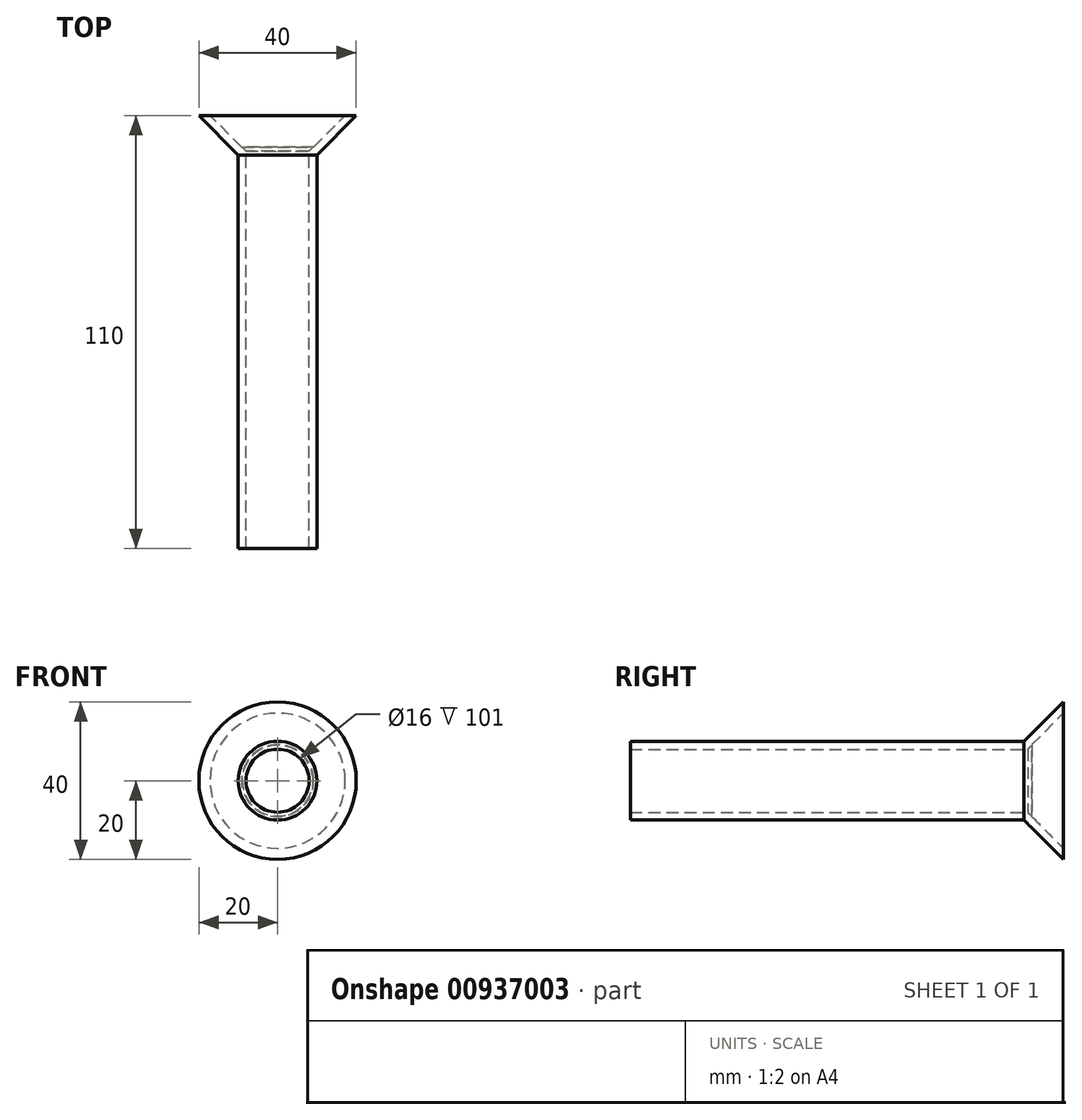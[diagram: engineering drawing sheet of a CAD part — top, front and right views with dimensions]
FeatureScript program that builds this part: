
annotation { "Feature Type Name" : "Feature", "Feature Type Description" : "" }
export const myFeature = defineFeature(function(context is Context, id is Id, definition is map)
    precondition{}
    {
        {
            var Q0;
            Q0=qCreatedBy(makeId("Front.planeOp"),FACE);
            var sketch = newSketch(context, id + "F0", { "sketchPlane" : qUnion([Q0])});
            skCircle(sketch, "E0", {"center": v(0, 0) * mm, "radius": 8 * mm});
            skCircle(sketch, "E1", {"center": v(0, 0) * mm, "radius": 10 * mm});
            skSolve(sketch);
        }
        {
            var Q0;
            Q0 = qSketchRegion(id + "F0", true);
            extrude(context, id + "F1", {"entities" : qUnion([Q0]), "depth" : 100 * mm, "offsetDistance" : 25 * mm});
        }
        {
            var Q0;
            Q0=qCreatedBy(makeId("Right.planeOp"),FACE);
            var sketch = newSketch(context, id + "F2", { "sketchPlane" : qUnion([Q0])});
            skLineSegment(sketch, "E2", {"start": v(0, 0) * mm, "end": v(15.72, 0) * mm, "construction": true});
            skLineSegment(sketch, "E3", {"start": v(0, 0) * mm, "end": v(0, -10) * mm});
            skLineSegment(sketch, "E4", {"start": v(0, -10) * mm, "end": v(10, -20) * mm});
            skLineSegment(sketch, "E5", {"start": v(10, -20) * mm, "end": v(10, -17.17) * mm});
            skLineSegment(sketch, "E6", {"start": v(10, -17.17) * mm, "end": v(2, -9.17) * mm});
            skLineSegment(sketch, "E7", {"start": v(2, -9.17) * mm, "end": v(2, -8) * mm});
            skLineSegment(sketch, "E8.0", {"start": v(0, -8) * mm, "end": v(0, 8) * mm, "construction": true});
            skLineSegment(sketch, "E9.0", {"start": v(0, -10) * mm, "end": v(0, 10) * mm, "construction": true});
            skLineSegment(sketch, "E10", {"start": v(0, -8) * mm, "end": v(2, -8) * mm});
            skSolve(sketch);
        }
        {
            var Q0;
            Q0 = qSketchRegion(id + "F2", true);
            var Q1;
            Q1=sQuery(id+"F2.wireOp",EDGE,"E2");
            revolve(context, id + "F3", {"operationType" : NewBodyOperationType.ADD, "surfaceOperationType" : NewSurfaceOperationType.NEW, "entities" : qUnion([Q0]), "axis" : qUnion([Q1]), "revolveType" : RevolveType.FULL});
        }
        {
            var Q0;
            Q0=makeQuery(id+"F3.opRevolve","SWEPT_EDGE",EDGE,{"disambiguationData":[OSD([sQuery(id+"F2.wireOp",EDGE,"E7"),sQuery(id+"F2.wireOp",EDGE,"E10")])]});
            chamfer(context, id + "F4", {"entities" : qUnion([Q0]), "width" : 1 * mm, "tangentPropagation" : true});
        }
    });
